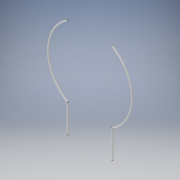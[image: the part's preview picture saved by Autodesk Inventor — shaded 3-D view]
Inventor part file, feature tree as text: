
AUTODESK INVENTOR PART (.ipt)
format: ipt  version: 2017 (Build 210142000, 142)  size: 137,728 bytes
history: native  units: in
note: dims shown in document units (in); Inventor stores cm internally (conversion verified against a paired STEP export)
features: sketch x7, plane x5, sweep x2, extrude x2
ambient origin geometry x8: Origin, YZ Plane, XZ Plane, XY Plane, X Axis, Y Axis, Z Axis, Center Point
bodies: Solid1 (feature_tree)
feature tree (16):
  sketch  "Sketch1"  dims[d3=0.25in d4=0.25in]
  plane  "Work Plane5"
  plane  "Work Plane6"
  sketch  "Sketch4"  dims[d5=0.0in d6=0.0in d7=0.0in d8=0.0in]
  sketch  "Sketch5"  dims[d9=5.0in d10=5.0in]
  sweep  "Sweep1"
  sweep  "Sweep2"
  plane  "Work Plane7"
  sketch  "Sketch6"  dims[d11=0.25in d12=5.0in d13=0.0in]
  sketch  "Sketch7"  dims[d14=5.0in]
  plane  "Work Plane8"
  extrude  "Extrusion1"  Depth=5.0in
  plane  "Work Plane10"
  extrude  "Extrusion2"  Depth=5.0in TaperAngle=0.0deg
  sketch  "Sketch8"  dims[d15=0.25in]
  sketch  "Sketch9"  dims[d16=5.0in d17=0.0in]
